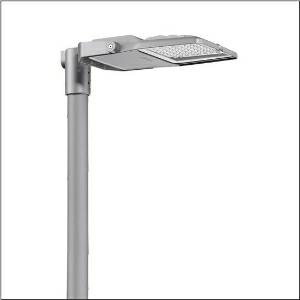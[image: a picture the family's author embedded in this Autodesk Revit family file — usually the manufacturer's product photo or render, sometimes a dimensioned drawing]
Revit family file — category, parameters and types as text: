
# Revit family: floodlight_fl_21_mini___pl64_5xa7776c2e3a_3ffb
name_source: partatom
category: Lighting Fixtures
units: mm (PartAtom-declared; Revit-internal decimal feet)

## family parameters
Cut with Voids When Loaded = No
Host = Face
Light Source = No
Part Type = Normal
Room Calculation Point = No
Round Connector Dimension = Use Diameter
Shared = No

## types (1)
- --- (1 x LED, 11770 lm, 89 W, 3000K)
    Apparent Load = 89 VA
    CIE Flux Codes = 28 80 98 100 100
    Color Rendering = 70
    Color Temperature = 3000K
    Default Elevation = 1800 mm
    Description = Floodlight FL 21 mini, floodlight, primary light control with lens, of PMMA, primary optical cover: protective disc, of toughened safety glass, transparent, light distribution: PL64, light emission: direct distribution, installation type: surface-mounted, LED, High Power LED, rated luminous flux: 11.770lm, luminous efficacy: 132lm/W, light colour: 730, colour temperature: 3000K, control gear: Smart Interface (Zhaga), control: flexible luminous flux parameterisation, time-dependent luminous flux control, constant luminous flux control, overheat protection, pre-setting: logarithmic dimming characteristic, with terminal, 6-pole, mains connection: 220..240V, AC, 50/60Hz, start of lifetime: 89W, end of service life: 94W, reduction: 43W, luminaire housing, of diecast aluminium, powder-coated, SITECO metallic grey (DB 702S), corrosivity category C5 mid according to DIN EN ISO 12944, suitable for swimming pools, chlorine-resistant, sealing non-destructively replaceable, please order mast flange separately, mast bracket, of steel, galvanised, powder-coated, SITECO metallic grey (DB 702S), Smart Interface below and above, protection rating (complete): IP66, insulation class (complete): insulation class II (safety insulation), certification: CE, ENEC, VDE, protection symbol: D, impact resistance: IK08, permissible operating ambient temperature: -40..+40°C, permissible operating ambient temperature for outdoor applications: -40..+50°C, standard: DIN EN 12944, LABS conformity tested according to VDMA 24364:2018-05, packaging unit: 1 piece

Light Distribution: PL64
    Height = 70 mm
    Lamp = 1 x LED
    Lamp Light Flux = 11770 lm
    Lamp Power = 89 W
    Lamp count = 1
    Length = 485 mm
    Luminous efficacy = 132 lm/W
    Manufacturer = Siteco
    ModVariant = No
    Model = 5XA7776C2E3A
    Number of Poles = 1
    OnlyDefault = Yes
    Power Factor = 1
    Product Name = Floodlight FL 21 mini | PL64
    Product group = floodlight | pylon annexe
    ProductGroupID = 6201
    Protection Class = Protection class II
    Protection Degree = IP 66
    RLX_Detail_Level = 1
    RLX_Emergency_Light_Flux = 0 lm
    RLX_Emergency_Type = 0
    RLX_Emergency_Type_DB = No
    RlxData = <blob elided: 101145 chars, md5=85dae60f>
    Socket = socket
    Standby Power = 0 W
    System Light Flux = 11770 lm
    System Power = 89 W
    Type Comments = factory setting: luminous flux: 100 % | dim-lin: 254 | 456 mA
    Type Image = l_1007125.jpg
    URL = http://relux.com
    VarID = @adj_164817
    Voltage = 0 V
    Weight = 0.00 kg
    Width = 337 mm

## geometry (parser evidence)
native form markers: Blend x4, Sweep x12
no freeform markers — native parametric forms only
